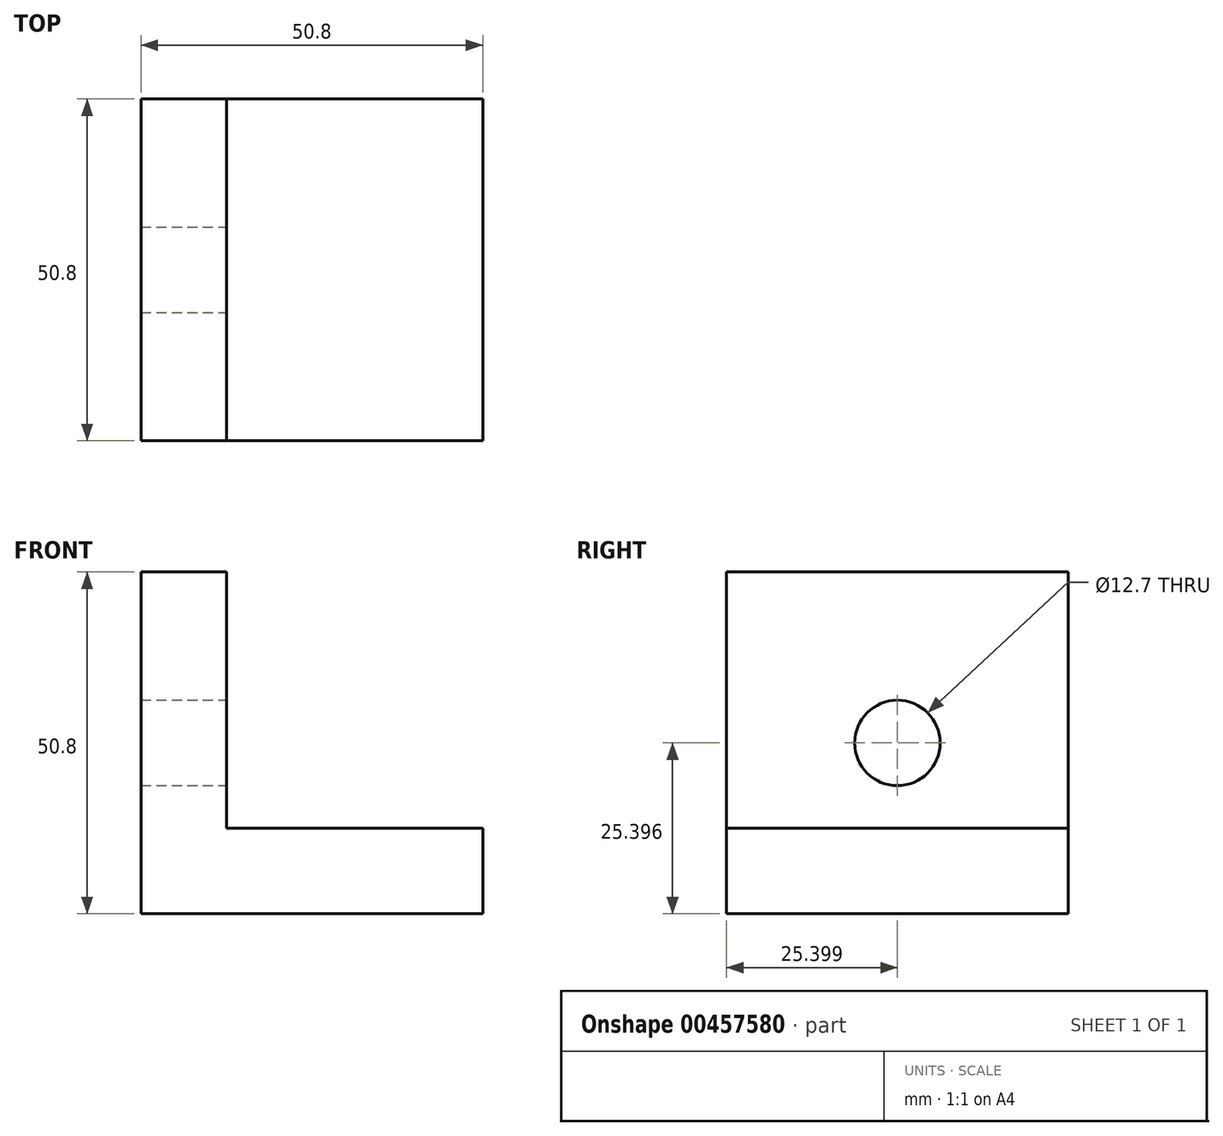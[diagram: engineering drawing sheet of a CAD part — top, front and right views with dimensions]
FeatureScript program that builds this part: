
annotation { "Feature Type Name" : "Feature", "Feature Type Description" : "" }
export const myFeature = defineFeature(function(context is Context, id is Id, definition is map)
    precondition{}
    {
        {
            var Q0;
            Q0=qCreatedBy(makeId("Right.planeOp"),FACE);
            var sketch = newSketch(context, id + "F0", { "sketchPlane" : qUnion([Q0])});
            skLineSegment(sketch, "E0.bottom", {"start": v(-27.7, 56.86) * mm, "end": v(23.1, 56.86) * mm});
            skLineSegment(sketch, "E0.top", {"start": v(-27.7, 6.06) * mm, "end": v(23.1, 6.06) * mm});
            skLineSegment(sketch, "E0.left", {"start": v(-27.7, 56.86) * mm, "end": v(-27.7, 6.06) * mm});
            skLineSegment(sketch, "E0.right", {"start": v(23.1, 56.86) * mm, "end": v(23.1, 6.06) * mm});
            skCircle(sketch, "E1", {"center": v(-2.3, 31.46) * mm, "radius": 6.35 * mm});
            skSolve(sketch);
        }
        {
            var Q0;
            Q0=makeQuery(id+"F0.imprint","IMPRINT",FACE,{"disambiguationData":[TD([[makeQuery(id+"F0.imprint","IMPRINT",EDGE,{"derivedFrom":sQuery(id+"F0.wireOp",EDGE,"E0.bottom")}),-1.0]])]});
            extrude(context, id + "F1", {"entities" : qUnion([Q0]), "oppositeDirection" : true, "depth" : 12.7 * mm});
        }
        {
            var Q0;
            Q0=makeQuery(id+"F1.opExtrude","CAP_FACE",FACE,{"disambiguationData":[OSD([sQuery(id+"F0.wireOp",EDGE,"E0.bottom"),sQuery(id+"F0.wireOp",EDGE,"E0.top"),sQuery(id+"F0.wireOp",EDGE,"E0.left"),sQuery(id+"F0.wireOp",EDGE,"E0.right")])],"isStart":true});
            var sketch = newSketch(context, id + "F2", { "sketchPlane" : qUnion([Q0])});
            skLineSegment(sketch, "E2.bottom", {"start": v(-27.7, 6.06) * mm, "end": v(23.1, 6.06) * mm});
            skLineSegment(sketch, "E2.top", {"start": v(-27.7, 18.76) * mm, "end": v(23.1, 18.76) * mm});
            skLineSegment(sketch, "E2.left", {"start": v(-27.7, 6.06) * mm, "end": v(-27.7, 18.76) * mm});
            skLineSegment(sketch, "E2.right", {"start": v(23.1, 6.06) * mm, "end": v(23.1, 18.76) * mm});
            skSolve(sketch);
        }
        {
            var Q0;
            Q0=makeQuery(id+"F2.imprint","IMPRINT",FACE,{"disambiguationData":[TD([[makeQuery(id+"F2.imprint","IMPRINT",EDGE,{"derivedFrom":sQuery(id+"F2.wireOp",EDGE,"E2.bottom")}),1.0]])]});
            extrude(context, id + "F3", {"entities" : qUnion([Q0]), "operationType" : NewBodyOperationType.ADD, "depth" : 38.1 * mm});
        }
    });
